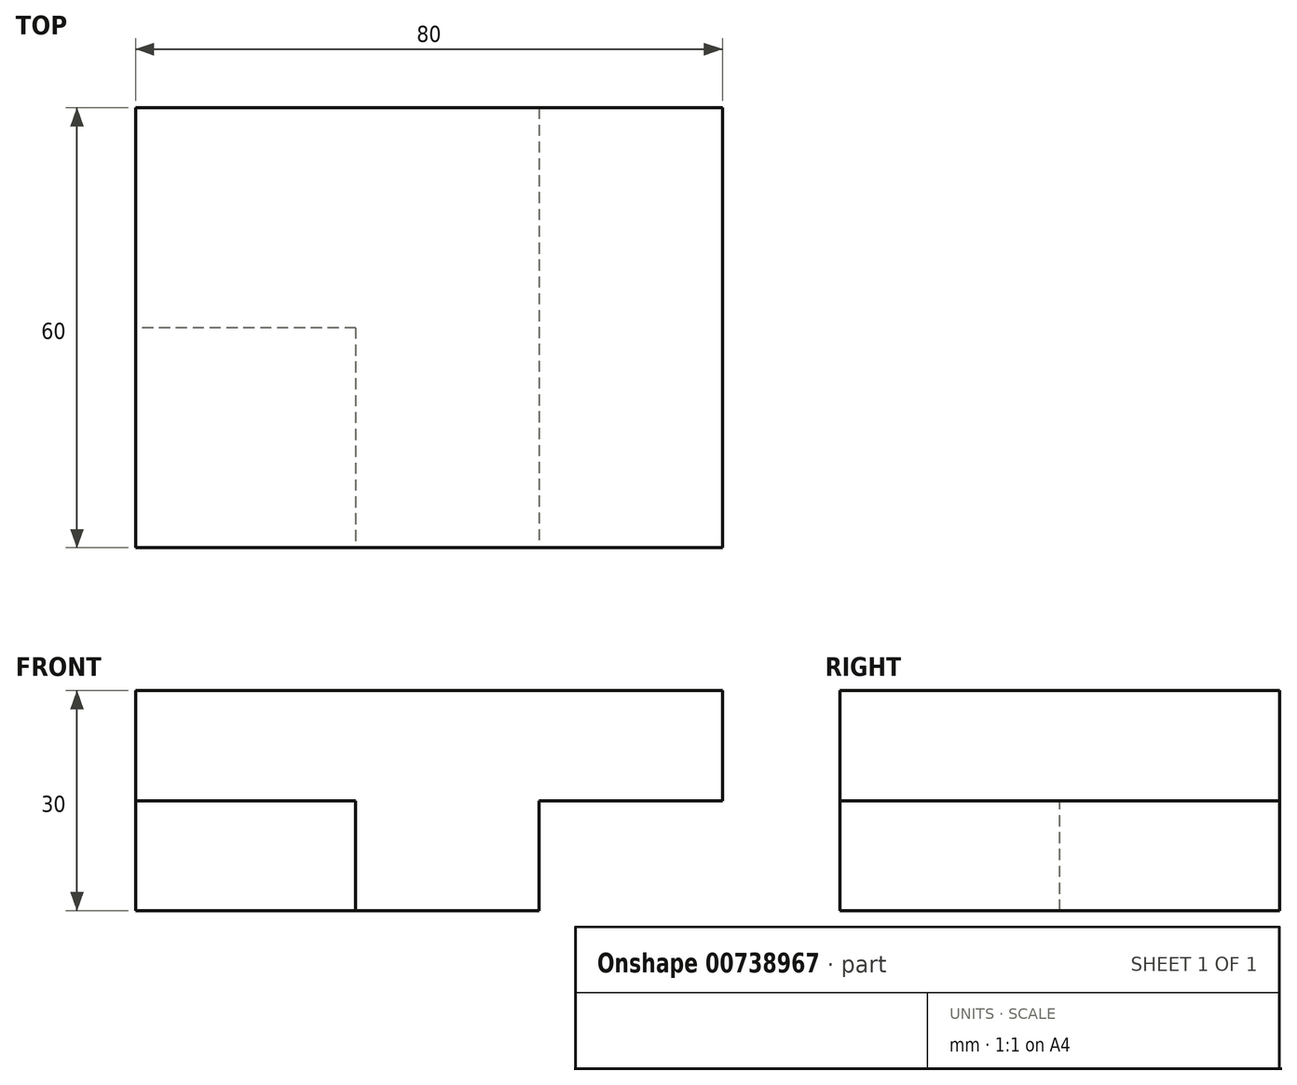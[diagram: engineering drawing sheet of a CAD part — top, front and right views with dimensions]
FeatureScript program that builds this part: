
annotation { "Feature Type Name" : "Feature", "Feature Type Description" : "" }
export const myFeature = defineFeature(function(context is Context, id is Id, definition is map)
    precondition{}
    {
        {
            var Q0;
            Q0=qCreatedBy(makeId("Front.planeOp"),FACE);
            var sketch = newSketch(context, id + "F0", { "sketchPlane" : qUnion([Q0])});
            skLineSegment(sketch, "E0.bottom", {"start": v(0, 0) * mm, "end": v(-80, 0) * mm});
            skLineSegment(sketch, "E0.top", {"start": v(0, 30) * mm, "end": v(-80, 30) * mm});
            skLineSegment(sketch, "E0.left", {"start": v(0, 0) * mm, "end": v(0, 30) * mm});
            skLineSegment(sketch, "E0.right", {"start": v(-80, 0) * mm, "end": v(-80, 30) * mm});
            skSolve(sketch);
        }
        {
            var Q0;
            Q0=makeQuery(id+"F0.imprint","IMPRINT",FACE,{"disambiguationData":[TD([[makeQuery(id+"F0.imprint","IMPRINT",EDGE,{"derivedFrom":sQuery(id+"F0.wireOp",EDGE,"E0.bottom")}),-1.0]])]});
            extrude(context, id + "F1", {"entities" : qUnion([Q0]), "depth" : 60 * mm, "offsetDistance" : 25 * mm});
        }
        {
            var Q0;
            Q0=makeQuery(id+"F1.opExtrude","CAP_FACE",FACE,{"disambiguationData":[OSD([sQuery(id+"F0.wireOp",EDGE,"E0.bottom"),sQuery(id+"F0.wireOp",EDGE,"E0.top"),sQuery(id+"F0.wireOp",EDGE,"E0.left"),sQuery(id+"F0.wireOp",EDGE,"E0.right")])],"isStart":false});
            var sketch = newSketch(context, id + "F2", { "sketchPlane" : qUnion([Q0])});
            skLineSegment(sketch, "E1", {"start": v(-80, 15) * mm, "end": v(-50, 15) * mm});
            skLineSegment(sketch, "E2", {"start": v(-50, 15) * mm, "end": v(-50, 0) * mm});
            skLineSegment(sketch, "E3", {"start": v(-50, 0) * mm, "end": v(-80, 0) * mm});
            skLineSegment(sketch, "E4", {"start": v(-80, 0) * mm, "end": v(-80, 15) * mm});
            skLineSegment(sketch, "E5", {"start": v(0, 15) * mm, "end": v(-25, 15) * mm});
            skLineSegment(sketch, "E6", {"start": v(-25, 15) * mm, "end": v(-25, 0) * mm});
            skLineSegment(sketch, "E7", {"start": v(-25, 0) * mm, "end": v(0, 0) * mm});
            skLineSegment(sketch, "E8", {"start": v(0, 0) * mm, "end": v(0, 15) * mm});
            skSolve(sketch);
        }
        {
            var Q0;
            Q0=makeQuery(id+"F2.imprint","IMPRINT",FACE,{"disambiguationData":[TD([[makeQuery(id+"F2.imprint","IMPRINT",EDGE,{"derivedFrom":sQuery(id+"F2.wireOp",EDGE,"E1")}),-1.0]])]});
            extrude(context, id + "F3", {"entities" : qUnion([Q0]), "operationType" : NewBodyOperationType.REMOVE, "oppositeDirection" : true, "depth" : 30 * mm, "offsetDistance" : 25 * mm});
        }
        {
            var Q0;
            Q0=makeQuery(id+"F2.imprint","IMPRINT",FACE,{"disambiguationData":[TD([[makeQuery(id+"F2.imprint","IMPRINT",EDGE,{"derivedFrom":sQuery(id+"F2.wireOp",EDGE,"E5")}),1.0]])]});
            extrude(context, id + "F4", {"entities" : qUnion([Q0]), "operationType" : NewBodyOperationType.REMOVE, "endBound" : BoundingType.THROUGH_ALL, "oppositeDirection" : true, "depth" : 25 * mm, "offsetDistance" : 25 * mm});
        }
    });
